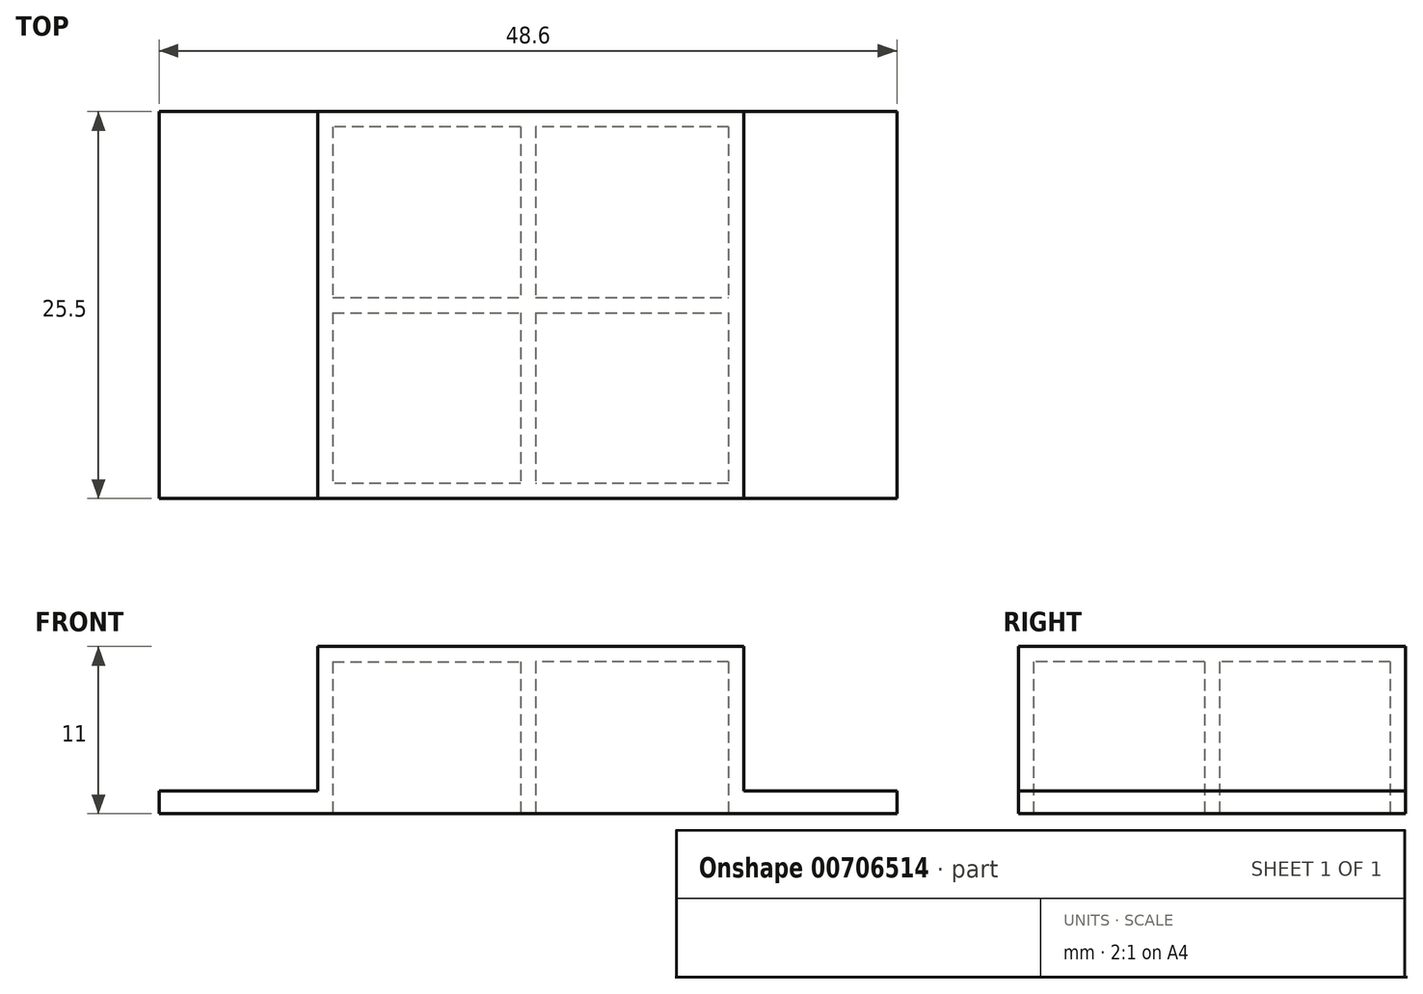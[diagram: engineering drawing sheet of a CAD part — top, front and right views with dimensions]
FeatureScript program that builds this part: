
annotation { "Feature Type Name" : "Feature", "Feature Type Description" : "" }
export const myFeature = defineFeature(function(context is Context, id is Id, definition is map)
    precondition{}
    {
        {
            var Q0;
            Q0=qCreatedBy(makeId("Top.planeOp"),FACE);
            var sketch = newSketch(context, id + "F0", { "sketchPlane" : qUnion([Q0])});
            skLineSegment(sketch, "E0.bottom", {"start": v(24.3, 12.75) * mm, "end": v(-24.3, 12.75) * mm});
            skLineSegment(sketch, "E0.top", {"start": v(24.3, -12.75) * mm, "end": v(-24.3, -12.75) * mm});
            skLineSegment(sketch, "E0.left", {"start": v(24.3, 12.75) * mm, "end": v(24.3, -12.75) * mm});
            skLineSegment(sketch, "E0.right", {"start": v(-24.3, 12.75) * mm, "end": v(-24.3, -12.75) * mm});
            skPoint(sketch, "E0.middle", {"position": v(0, 0) * mm});
            skLineSegment(sketch, "E1", {"start": v(-12.86, 11.75) * mm, "end": v(-12.86, 0.5) * mm});
            skLineSegment(sketch, "E2.0", {"start": v(23.3, 11.75) * mm, "end": v(23.3, -11.75) * mm});
            skLineSegment(sketch, "E2.1", {"start": v(23.3, 11.75) * mm, "end": v(14.2, 11.75) * mm});
            skLineSegment(sketch, "E2.2", {"start": v(-23.3, 11.75) * mm, "end": v(-23.3, -11.75) * mm});
            skLineSegment(sketch, "E2.3", {"start": v(23.3, -11.75) * mm, "end": v(14.2, -11.75) * mm});
            skLineSegment(sketch, "E3", {"start": v(14.2, 11.75) * mm, "end": v(14.2, -11.75) * mm});
            skLineSegment(sketch, "E4", {"start": v(13.2, 11.75) * mm, "end": v(13.2, 0.5) * mm});
            skLineSegment(sketch, "E5", {"start": v(-12.86, 0.5) * mm, "end": v(-0.5, 0.5) * mm});
            skLineSegment(sketch, "E6", {"start": v(-12.86, -0.5) * mm, "end": v(-0.5, -0.5) * mm});
            skLineSegment(sketch, "E7", {"start": v(-13.86, 12.75) * mm, "end": v(-13.86, -12.75) * mm});
            skLineSegment(sketch, "E8", {"start": v(-0.5, 11.75) * mm, "end": v(-0.5, 0.5) * mm});
            skLineSegment(sketch, "E9", {"start": v(0.5, 11.75) * mm, "end": v(0.5, 0.5) * mm});
            skLineSegment(sketch, "E10", {"start": v(14.2, -11.75) * mm, "end": v(14.2, -12.75) * mm});
            skLineSegment(sketch, "E11", {"start": v(13.7, -12.25) * mm, "end": v(-13.36, -12.25) * mm});
            skLineSegment(sketch, "E12", {"start": v(13.7, -12.25) * mm, "end": v(13.7, 12.25) * mm});
            skLineSegment(sketch, "E13", {"start": v(13.7, 12.25) * mm, "end": v(-13.36, 12.25) * mm});
            skLineSegment(sketch, "E14", {"start": v(-13.36, 12.25) * mm, "end": v(-13.36, -12.25) * mm});
            skPoint(sketch, "E15.orphan", {"position": v(-13.86, 12.25) * mm});
            skPoint(sketch, "E16.orphan", {"position": v(14.2, -12.25) * mm});
            skLineSegment(sketch, "E17.trimOffspring", {"start": v(13.2, -11.75) * mm, "end": v(0.5, -11.75) * mm});
            skPoint(sketch, "E18.trimOffspring.end.orphan", {"position": v(0, -12.75) * mm});
            skLineSegment(sketch, "E19.trimOffspring", {"start": v(-13.86, -11.75) * mm, "end": v(-23.3, -11.75) * mm});
            skPoint(sketch, "E20.orphan", {"position": v(0, 12.75) * mm});
            skLineSegment(sketch, "E21.trimOffspring", {"start": v(13.2, 11.75) * mm, "end": v(0.5, 11.75) * mm});
            skLineSegment(sketch, "E22", {"start": v(14.2, 11.75) * mm, "end": v(14.2, 12.75) * mm});
            skLineSegment(sketch, "E23.trimOffspring", {"start": v(-12.86, -0.5) * mm, "end": v(-12.86, -11.75) * mm});
            skLineSegment(sketch, "E24.trimOffspring", {"start": v(-0.5, -0.5) * mm, "end": v(-0.5, -11.75) * mm});
            skLineSegment(sketch, "E25.trimOffspring", {"start": v(0.5, 0.5) * mm, "end": v(13.2, 0.5) * mm});
            skLineSegment(sketch, "E26.trimOffspring", {"start": v(0.5, -0.5) * mm, "end": v(0.5, -11.75) * mm});
            skLineSegment(sketch, "E27.trimOffspring", {"start": v(0.5, -0.5) * mm, "end": v(13.2, -0.5) * mm});
            skLineSegment(sketch, "E28.trimOffspring", {"start": v(13.2, -0.5) * mm, "end": v(13.2, -11.75) * mm});
            skLineSegment(sketch, "E29.trimOffspring", {"start": v(-0.5, 11.75) * mm, "end": v(-12.86, 11.75) * mm});
            skLineSegment(sketch, "E30.trimOffspring", {"start": v(-13.86, 11.75) * mm, "end": v(-23.3, 11.75) * mm});
            skLineSegment(sketch, "E31.trimOffspring", {"start": v(-0.5, -11.75) * mm, "end": v(-12.86, -11.75) * mm});
            skSolve(sketch);
        }
        {
            var Q0;
            Q0=makeQuery(id+"F0.imprint","IMPRINT",FACE,{"disambiguationData":[TD([[makeQuery(id+"F0.imprint","IMPRINT",EDGE,{"derivedFrom":sQuery(id+"F0.wireOp",EDGE,"E2.0")}),-1.0]])]});
            var Q1;
            {var subQ0=sQuery(id+"F0.wireOp",EDGE,"E0.left");Q1=makeQuery(id+"F0.imprint","IMPRINT",FACE,{"disambiguationData":[TD([[makeQuery(id+"F0.imprint","IMPRINT",EDGE,{"derivedFrom":subQ0}),-1.0]])]});}
            var Q2;
            {var subQ1=sQuery(id+"F0.wireOp",EDGE,"E0.right");Q2=makeQuery(id+"F0.imprint","IMPRINT",FACE,{"disambiguationData":[TD([[makeQuery(id+"F0.imprint","IMPRINT",EDGE,{"derivedFrom":subQ1}),1.0]])]});}
            var Q3;
            {var subQ0=sQuery(id+"F0.wireOp",EDGE,"E2.2");Q3=makeQuery(id+"F0.imprint","IMPRINT",FACE,{"disambiguationData":[TD([[makeQuery(id+"F0.imprint","IMPRINT",EDGE,{"derivedFrom":subQ0}),1.0]])]});}
            extrude(context, id + "F1", {"entities" : qUnion([Q0, Q1, Q2, Q3]), "depth" : 1.5 * mm, "offsetDistance" : 25 * mm});
        }
        {
            var Q0;
            Q0=makeQuery(id+"F0.imprint","IMPRINT",FACE,{"disambiguationData":[TD([[makeQuery(id+"F0.imprint","IMPRINT",EDGE,{"derivedFrom":sQuery(id+"F0.wireOp",EDGE,"E3")}),-1.0]])]});
            extrude(context, id + "F2", {"entities" : qUnion([Q0]), "operationType" : NewBodyOperationType.ADD, "depth" : 6 * mm, "offsetDistance" : 25 * mm});
        }
        {
            var Q0;
            Q0=makeQuery(id+"F0.imprint","IMPRINT",FACE,{"disambiguationData":[TD([[makeQuery(id+"F0.imprint","IMPRINT",EDGE,{"derivedFrom":sQuery(id+"F0.wireOp",EDGE,"E1")}),-1.0]])]});
            extrude(context, id + "F3", {"entities" : qUnion([Q0]), "operationType" : NewBodyOperationType.ADD, "depth" : 10 * mm, "offsetDistance" : 25 * mm});
        }
        {
            var Q0;
            Q0=makeQuery(id+"F2.opExtrude","CAP_FACE",FACE,{"disambiguationData":[OSD([sQuery(id+"F0.wireOp",EDGE,"E0.bottom"),sQuery(id+"F0.wireOp",EDGE,"E0.top"),sQuery(id+"F0.wireOp",EDGE,"E3"),sQuery(id+"F0.wireOp",EDGE,"E7"),sQuery(id+"F0.wireOp",EDGE,"E10"),sQuery(id+"F0.wireOp",EDGE,"E11"),sQuery(id+"F0.wireOp",EDGE,"E12"),sQuery(id+"F0.wireOp",EDGE,"E13"),sQuery(id+"F0.wireOp",EDGE,"E14"),sQuery(id+"F0.wireOp",EDGE,"E22")])],"isStart":false});
            var sketch = newSketch(context, id + "F4", { "sketchPlane" : qUnion([Q0])});
            skLineSegment(sketch, "E32.bottom", {"start": v(-13.36, 12.25) * mm, "end": v(13.7, 12.25) * mm});
            skLineSegment(sketch, "E32.top", {"start": v(-13.36, -12.25) * mm, "end": v(13.7, -12.25) * mm});
            skLineSegment(sketch, "E32.left", {"start": v(-13.36, 12.25) * mm, "end": v(-13.36, -12.25) * mm});
            skLineSegment(sketch, "E32.right", {"start": v(13.7, 12.25) * mm, "end": v(13.7, -12.25) * mm});
            skLineSegment(sketch, "E33.bottom", {"start": v(-13.86, 12.75) * mm, "end": v(14.2, 12.75) * mm});
            skLineSegment(sketch, "E33.top", {"start": v(-13.86, -12.75) * mm, "end": v(14.2, -12.75) * mm});
            skLineSegment(sketch, "E33.left", {"start": v(-13.86, 12.75) * mm, "end": v(-13.86, -12.75) * mm});
            skLineSegment(sketch, "E33.right", {"start": v(14.2, 12.75) * mm, "end": v(14.2, -12.75) * mm});
            skSolve(sketch);
        }
        {
            var Q0;
            Q0=qSketchRegion(id+"F4",true);
            extrude(context, id + "F5", {"entities" : qUnion([Q0]), "depth" : 4 * mm, "offsetDistance" : 25 * mm});
        }
        {
            var Q0;
            Q0=makeQuery(id+"F5.opExtrude","CAP_FACE",FACE,{"disambiguationData":[OSD([sQuery(id+"F4.wireOp",EDGE,"E32.bottom"),sQuery(id+"F4.wireOp",EDGE,"E32.top"),sQuery(id+"F4.wireOp",EDGE,"E32.left"),sQuery(id+"F4.wireOp",EDGE,"E32.right"),sQuery(id+"F4.wireOp",EDGE,"E33.bottom"),sQuery(id+"F4.wireOp",EDGE,"E33.top"),sQuery(id+"F4.wireOp",EDGE,"E33.left"),sQuery(id+"F4.wireOp",EDGE,"E33.right")])],"isStart":false});
            var sketch = newSketch(context, id + "F6", { "sketchPlane" : qUnion([Q0])});
            skLineSegment(sketch, "E34.bottom", {"start": v(-13.86, 12.75) * mm, "end": v(14.2, 12.75) * mm});
            skLineSegment(sketch, "E34.top", {"start": v(-13.86, -12.75) * mm, "end": v(14.2, -12.75) * mm});
            skLineSegment(sketch, "E34.left", {"start": v(-13.86, 12.75) * mm, "end": v(-13.86, -12.75) * mm});
            skLineSegment(sketch, "E34.right", {"start": v(14.2, 12.75) * mm, "end": v(14.2, -12.75) * mm});
            skSolve(sketch);
        }
        {
            var Q0;
            Q0=qSketchRegion(id+"F6",true);
            extrude(context, id + "F7", {"entities" : qUnion([Q0]), "operationType" : NewBodyOperationType.ADD, "depth" : 1 * mm, "offsetDistance" : 25 * mm});
        }
    });
